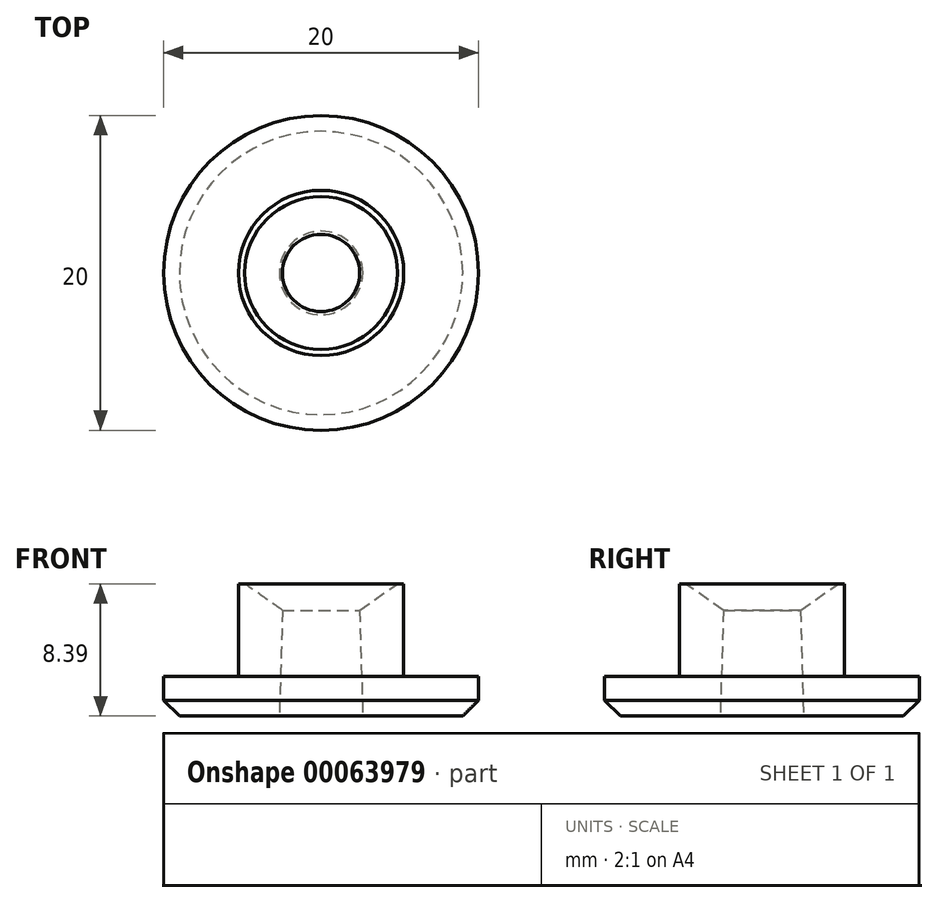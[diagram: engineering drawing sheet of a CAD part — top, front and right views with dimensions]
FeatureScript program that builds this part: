
annotation { "Feature Type Name" : "Feature", "Feature Type Description" : "" }
export const myFeature = defineFeature(function(context is Context, id is Id, definition is map)
    precondition{}
    {
        {
            var Q0;
            Q0=qCreatedBy(makeId("Front.planeOp"),FACE);
            var sketch = newSketch(context, id + "F0", { "sketchPlane" : qUnion([Q0])});
            skLineSegment(sketch, "E0", {"start": v(0, 0) * mm, "end": v(0, 7.5) * mm, "construction": true});
            skLineSegment(sketch, "E1", {"start": v(4.85, 8.4) * mm, "end": v(5.25, 8.4) * mm});
            skLineSegment(sketch, "E2", {"start": v(5.25, 8.4) * mm, "end": v(5.25, 2.5) * mm});
            skLineSegment(sketch, "E3", {"start": v(5.25, 2.5) * mm, "end": v(10, 2.5) * mm});
            skLineSegment(sketch, "E4", {"start": v(10, 2.5) * mm, "end": v(10, 0) * mm});
            skLineSegment(sketch, "E5", {"start": v(10, 0) * mm, "end": v(2.65, 0) * mm});
            skLineSegment(sketch, "E6", {"start": v(2.65, 0) * mm, "end": v(2.5, 5.07) * mm});
            skArc(sketch, "E7", {"start": v(2.5, 5.07) * mm, "mid": v(1.74, 6.8) * mm, "end": v(0, 7.5) * mm, "construction": true});
            skLineSegment(sketch, "E8", {"start": v(2.5, 5.07) * mm, "end": v(2.45, 6.72) * mm});
            skLineSegment(sketch, "E9", {"start": v(2.45, 6.72) * mm, "end": v(4.85, 8.4) * mm});
            skSolve(sketch);
        }
        {
            var Q0;
            Q0 = qSketchRegion(id + "F0", true);
            var Q1;
            Q1=sQuery(id+"F0.wireOp",EDGE,"E0");
            revolve(context, id + "F1", {"surfaceOperationType" : NewSurfaceOperationType.NEW, "entities" : qUnion([Q0]), "axis" : qUnion([Q1]), "revolveType" : RevolveType.FULL});
        }
        {
            var Q0;
            Q0=makeQuery(id+"F1.opRevolve","SWEPT_EDGE",EDGE,{"disambiguationData":[OSD([sQuery(id+"F0.wireOp",EDGE,"E4"),sQuery(id+"F0.wireOp",EDGE,"E5")])]});
            chamfer(context, id + "F2", {"entities" : qUnion([Q0]), "width" : 1 * mm, "tangentPropagation" : true});
        }
    });
